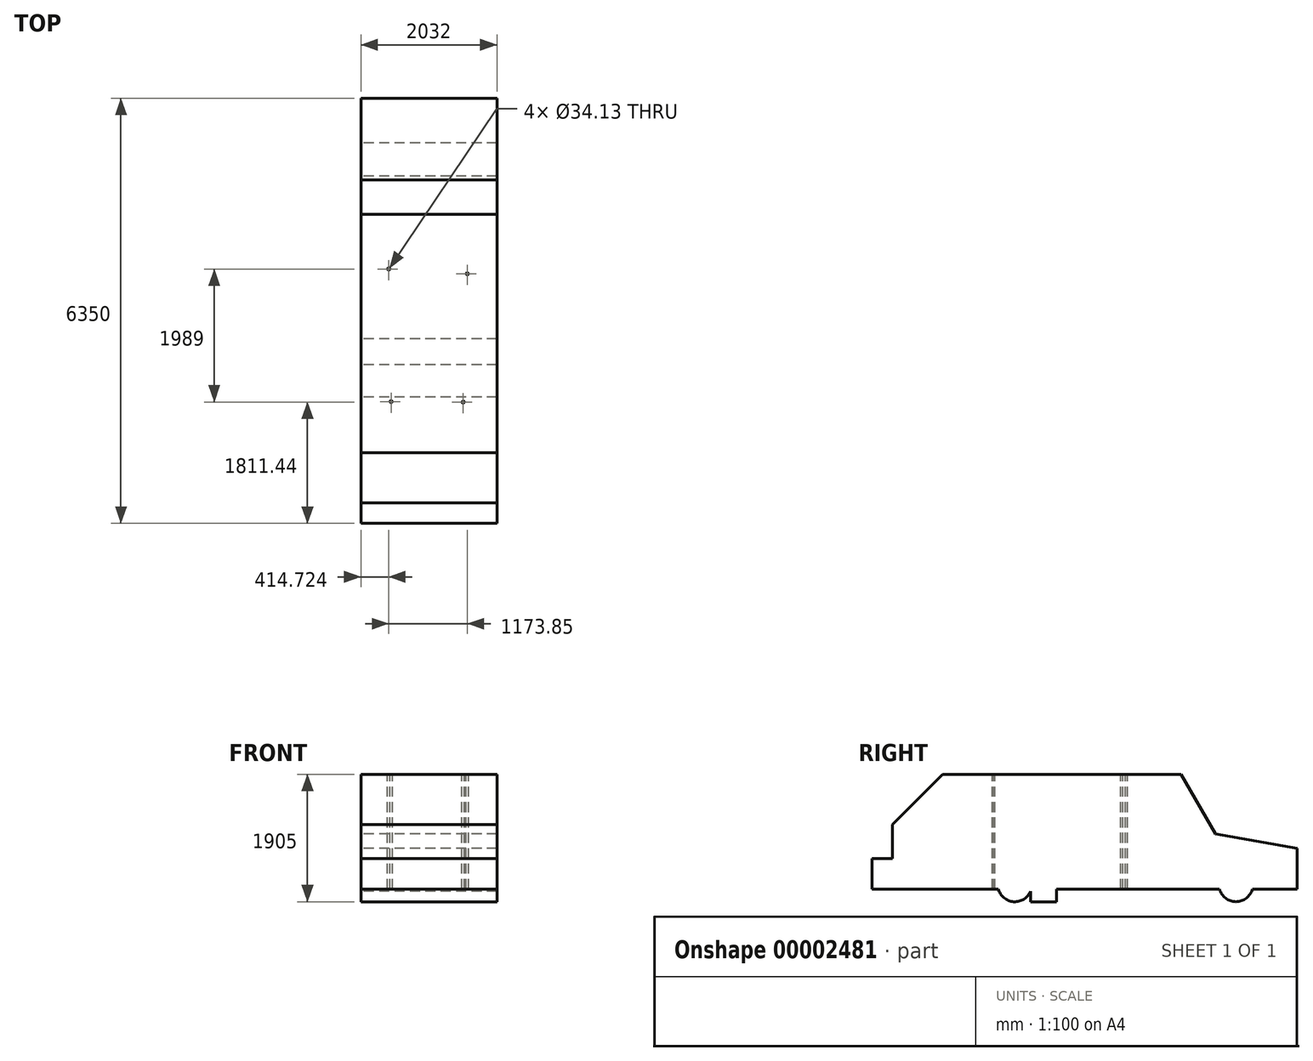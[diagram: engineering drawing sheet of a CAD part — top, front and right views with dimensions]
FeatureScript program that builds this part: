
annotation { "Feature Type Name" : "Feature", "Feature Type Description" : "" }
export const myFeature = defineFeature(function(context is Context, id is Id, definition is map)
    precondition{}
    {
        {
            var Q0;
            Q0=qCreatedBy(makeId("Right.planeOp"),FACE);
            var sketch = newSketch(context, id + "F0", { "sketchPlane" : qUnion([Q0])});
            skCircle(sketch, "E0", {"center": v(-1041.4, 254) * mm, "radius": 254 * mm});
            skCircle(sketch, "E1", {"center": v(2260.6, 254) * mm, "radius": 254 * mm});
            skLineSegment(sketch, "E2.bottom", {"start": v(-2120.9, 1905) * mm, "end": v(1442, 1905) * mm});
            skLineSegment(sketch, "E2.top", {"start": v(-3175, 190.5) * mm, "end": v(3175, 190.5) * mm});
            skLineSegment(sketch, "E2.left", {"start": v(-3175, 647.7) * mm, "end": v(-3175, 190.5) * mm});
            skLineSegment(sketch, "E2.right", {"start": v(3175, 800.1) * mm, "end": v(3175, 190.5) * mm});
            skLineSegment(sketch, "E3", {"start": v(-1041.4, 254) * mm, "end": v(2260.6, 254) * mm, "construction": true});
            skLineSegment(sketch, "E4", {"start": v(3175, 800.1) * mm, "end": v(1955.8, 1015.08) * mm});
            skLineSegment(sketch, "E5", {"start": v(1955.8, 1015.08) * mm, "end": v(1442, 1905) * mm});
            skLineSegment(sketch, "E6", {"start": v(-3175, 647.7) * mm, "end": v(-2870.2, 647.7) * mm});
            skLineSegment(sketch, "E7", {"start": v(-2870.2, 647.7) * mm, "end": v(-2870.2, 1155.7) * mm});
            skLineSegment(sketch, "E8", {"start": v(-2870.2, 1155.7) * mm, "end": v(-2120.9, 1905) * mm});
            skLineSegment(sketch, "E9", {"start": v(0, 0) * mm, "end": v(0, 190.5) * mm, "construction": true});
            skLineSegment(sketch, "E10.bottom", {"start": v(-806.43, 190.5) * mm, "end": v(-418.08, 190.5) * mm});
            skLineSegment(sketch, "E10.top", {"start": v(-806.43, 0) * mm, "end": v(-418.08, 0) * mm});
            skLineSegment(sketch, "E10.left", {"start": v(-806.43, 190.5) * mm, "end": v(-806.43, 0) * mm});
            skLineSegment(sketch, "E10.right", {"start": v(-418.08, 190.5) * mm, "end": v(-418.08, 0) * mm});
            skSolve(sketch);
        }
        {
            var Q0;
            Q0 = qSketchRegion(id + "F0", true);
            extrude(context, id + "F1", {"entities" : qUnion([Q0]), "depth" : 2032 * mm, "symmetric" : true});
        }
        {
            var Q0;
            Q0=makeQuery(id+"F1.opExtrude","SWEPT_FACE",FACE,{"disambiguationData":[OSD([sQuery(id+"F0.wireOp",EDGE,"E2.bottom")])]});
            var sketch = newSketch(context, id + "F2", { "sketchPlane" : qUnion([Q0])});
            skSolve(sketch);
        }
        {
            var Q0;
            {var subQ0=sQuery(id+"F0.wireOp",EDGE,"E2.bottom");Q0=makeQuery(id+"F2.imprint","IMPRINT",FACE,{"disambiguationData":[TD([[makeQuery(id+"F2.imprint","IMPRINT",EDGE,{"derivedFrom":makeQuery(id+"F1.opExtrude","CAP_EDGE",EDGE,{"disambiguationData":[OSD([subQ0])],"isStart":true})}),-1.0]])]});}
            var sketch = newSketch(context, id + "F3", { "sketchPlane" : qUnion([Q0])});
            skPoint(sketch, "E11", {"position": v(-564.67, -1357.18) * mm});
            skPoint(sketch, "E12", {"position": v(510.43, -1363.56) * mm});
            skPoint(sketch, "E13", {"position": v(572.58, 553.63) * mm});
            skPoint(sketch, "E14", {"position": v(-601.28, 625.44) * mm});
            skSolve(sketch);
        }
        {
            var Q0;
            Q0=sQuery(id+"F3.wireOp",VERTEX,"E11");
            var Q1;
            Q1=sQuery(id+"F3.wireOp",VERTEX,"E12");
            var Q2;
            Q2=sQuery(id+"F3.wireOp",VERTEX,"E13");
            var Q3;
            Q3=sQuery(id+"F3.wireOp",VERTEX,"E14");
            var Q4;
            Q4=makeQuery(id+"F1.opExtrude","SWEPT_BODY",BODY,{"disambiguationData":[OSD([sQuery(id+"F0.wireOp",EDGE,"E0"),sQuery(id+"F0.wireOp",EDGE,"E1"),sQuery(id+"F0.wireOp",EDGE,"E2.bottom"),sQuery(id+"F0.wireOp",EDGE,"E2.top"),sQuery(id+"F0.wireOp",EDGE,"E2.left"),sQuery(id+"F0.wireOp",EDGE,"E2.right"),sQuery(id+"F0.wireOp",EDGE,"E4"),sQuery(id+"F0.wireOp",EDGE,"E5"),sQuery(id+"F0.wireOp",EDGE,"E6"),sQuery(id+"F0.wireOp",EDGE,"E7"),sQuery(id+"F0.wireOp",EDGE,"E8"),sQuery(id+"F0.wireOp",EDGE,"E10.top"),sQuery(id+"F0.wireOp",EDGE,"E10.left"),sQuery(id+"F0.wireOp",EDGE,"E10.right")])]});
            hole(context, id + "F4", {"style" : HoleStyle.SIMPLE, "endStyle" : HoleEndStyle.THROUGH, "standardTappedOrClearance" : lookupTablePath({ "standard" : "ANSI", "engagement" : "75%", "pitch" : "6 tpi", "size" : "1 1/2", "type" : "Tapped" }), "standardBlindInLast" : lookupTablePath({ "standard" : "ANSI", "engagement" : "75%", "pitch" : "6 tpi", "size" : "1 1/2", "type" : "Tapped" }), "holeDiameter" : 34.13 * mm, "showTappedDepth" : true, "tappedDepth" : 12.7 * mm, "tapClearance" : 3, "locations" : qUnion([Q0, Q1, Q2, Q3]), "scope" : qUnion([Q4]), "majorDiameter" : 38.1 * mm});
        }
    });
